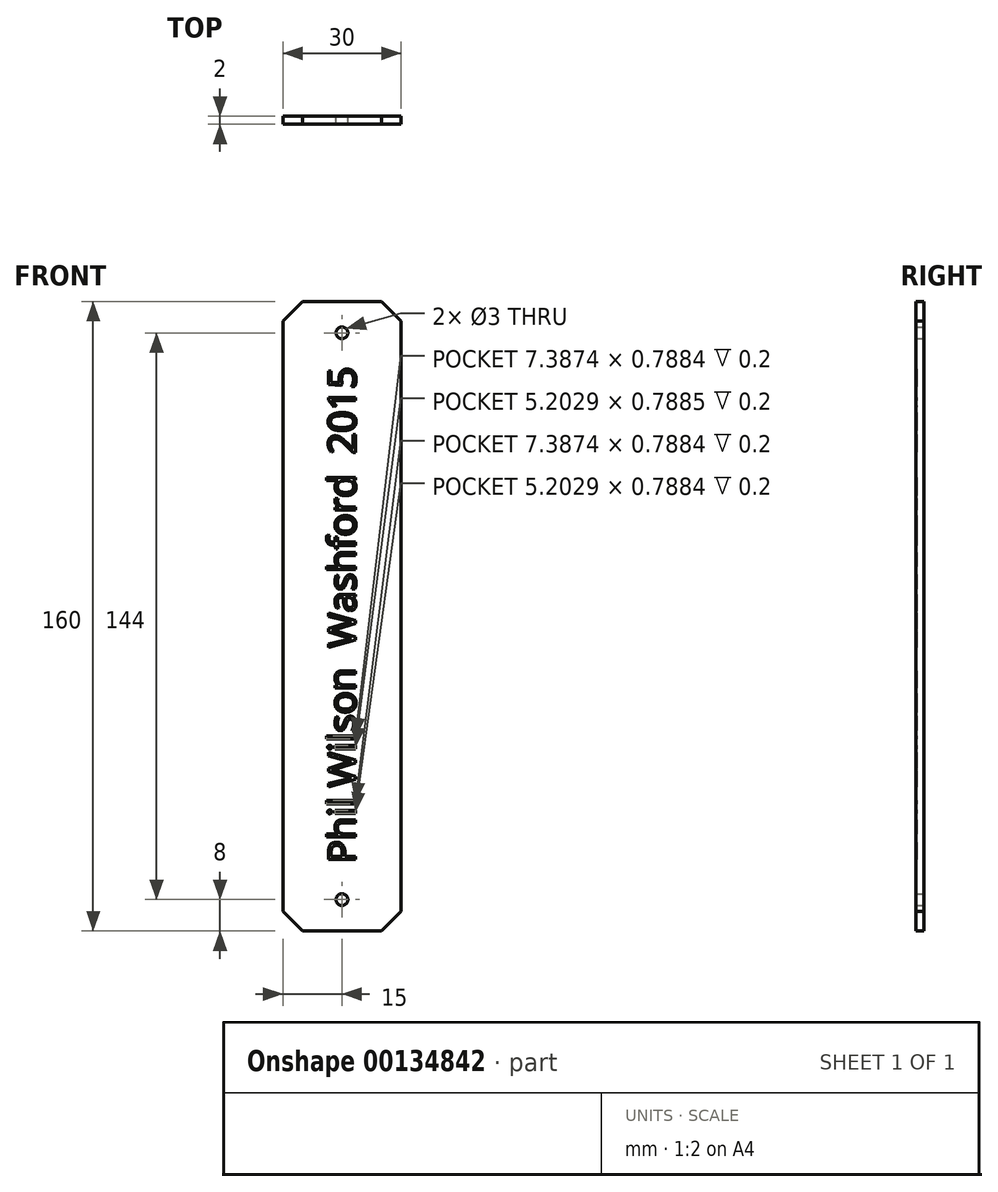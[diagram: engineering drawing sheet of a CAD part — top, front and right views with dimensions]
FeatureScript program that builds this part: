
annotation { "Feature Type Name" : "Feature", "Feature Type Description" : "" }
export const myFeature = defineFeature(function(context is Context, id is Id, definition is map)
    precondition{}
    {
        {
            var Q0;
            Q0=qCreatedBy(makeId("Front.planeOp"),FACE);
            var sketch = newSketch(context, id + "F0", { "sketchPlane" : qUnion([Q0])});
            skLineSegment(sketch, "E0.rect.bottom", {"start": v(80, -15) * mm, "end": v(-80, -15) * mm});
            skLineSegment(sketch, "E0.rect.top", {"start": v(80, 15) * mm, "end": v(-80, 15) * mm});
            skLineSegment(sketch, "E0.rect.left", {"start": v(80, -15) * mm, "end": v(80, 15) * mm});
            skLineSegment(sketch, "E0.rect.right", {"start": v(-80, -15) * mm, "end": v(-80, 15) * mm});
            skPoint(sketch, "E0.rect.middle", {"position": v(0, 0) * mm});
            skCircle(sketch, "E1", {"center": v(72, 0) * mm, "radius": 1.5 * mm});
            skPoint(sketch, "E1.centerSnap0", {"position": v(80, 0) * mm});
            skCircle(sketch, "E2", {"center": v(-72, 0) * mm, "radius": 1.5 * mm});
            skPoint(sketch, "E2.centerSnap0", {"position": v(-80, 0) * mm});
            skSolve(sketch);
        }
        {
            var Q0;
            Q0=qSketchRegion(id+"F0",true);
            extrude(context, id + "F1", {"entities" : qUnion([Q0]), "depth" : 2 * mm});
        }
        {
            var Q0;
            Q0=makeQuery(id+"F1.opExtrude","CAP_FACE",FACE,{"disambiguationData":[OSD([sQuery(id+"F0.wireOp",EDGE,"E0.rect.bottom"),sQuery(id+"F0.wireOp",EDGE,"E0.rect.top"),sQuery(id+"F0.wireOp",EDGE,"E0.rect.left"),sQuery(id+"F0.wireOp",EDGE,"E0.rect.right")])],"isStart":false});
            var sketch = newSketch(context, id + "F2", { "sketchPlane" : qUnion([Q0])});
            skText(sketch, "E3", { "text": "Phil Wilson  Washford  2015", "fontName": "OpenSans-Regular.ttf"});
            skPoint(sketch, "E4", {"position": v(62.77, 0) * mm});
            const initialGuessF2  = {"E3": [-0.06277, -0.0035, 1, 0, 0.007]};
            skSetInitialGuess(sketch, initialGuessF2);
            skSolve(sketch);
        }
        {
            var Q0;
            Q0=qSketchRegion(id+"F2",true);
            extrude(context, id + "F3", {"entities" : qUnion([Q0]), "operationType" : NewBodyOperationType.REMOVE, "oppositeDirection" : true, "depth" : 0.2 * mm});
        }
        {
            var Q0;
            Q0=makeQuery(id+"F1.opExtrude","SWEPT_BODY",BODY,{"disambiguationData":[OSD([sQuery(id+"F0.wireOp",EDGE,"E0.rect.bottom"),sQuery(id+"F0.wireOp",EDGE,"E0.rect.top"),sQuery(id+"F0.wireOp",EDGE,"E0.rect.left"),sQuery(id+"F0.wireOp",EDGE,"E0.rect.right")])]});
            var Q1;
            Q1=makeQuery(id+"F1.opExtrude","SWEPT_EDGE",EDGE,{"disambiguationData":[OSD([sQuery(id+"F0.wireOp",EDGE,"E0.rect.bottom"),sQuery(id+"F0.wireOp",EDGE,"E0.rect.right")])]});
            transform(context, id + "F4", {"entities" : qUnion([Q0]), "transformType" : TransformType.ROTATION, "transformAxis" : qUnion([Q1]), "angle" : 90 * degree, "oppositeDirection" : true, "makeCopy" : false});
        }
        {
            var Q0;
            Q0=makeQuery(id+"F1.opExtrude","SWEPT_EDGE",EDGE,{"disambiguationData":[OSD([sQuery(id+"F0.wireOp",EDGE,"E0.rect.top"),sQuery(id+"F0.wireOp",EDGE,"E0.rect.left")])]});
            var Q1;
            Q1=makeQuery(id+"F1.opExtrude","SWEPT_EDGE",EDGE,{"disambiguationData":[OSD([sQuery(id+"F0.wireOp",EDGE,"E0.rect.bottom"),sQuery(id+"F0.wireOp",EDGE,"E0.rect.left")])]});
            var Q2;
            Q2=makeQuery(id+"F1.opExtrude","SWEPT_EDGE",EDGE,{"disambiguationData":[OSD([sQuery(id+"F0.wireOp",EDGE,"E0.rect.top"),sQuery(id+"F0.wireOp",EDGE,"E0.rect.right")])]});
            var Q3;
            Q3=makeQuery(id+"F1.opExtrude","SWEPT_EDGE",EDGE,{"disambiguationData":[OSD([sQuery(id+"F0.wireOp",EDGE,"E0.rect.bottom"),sQuery(id+"F0.wireOp",EDGE,"E0.rect.right")])]});
            chamfer(context, id + "F5", {"entities" : qUnion([Q0, Q1, Q2, Q3]), "width" : 5 * mm, "tangentPropagation" : true});
        }
    });
